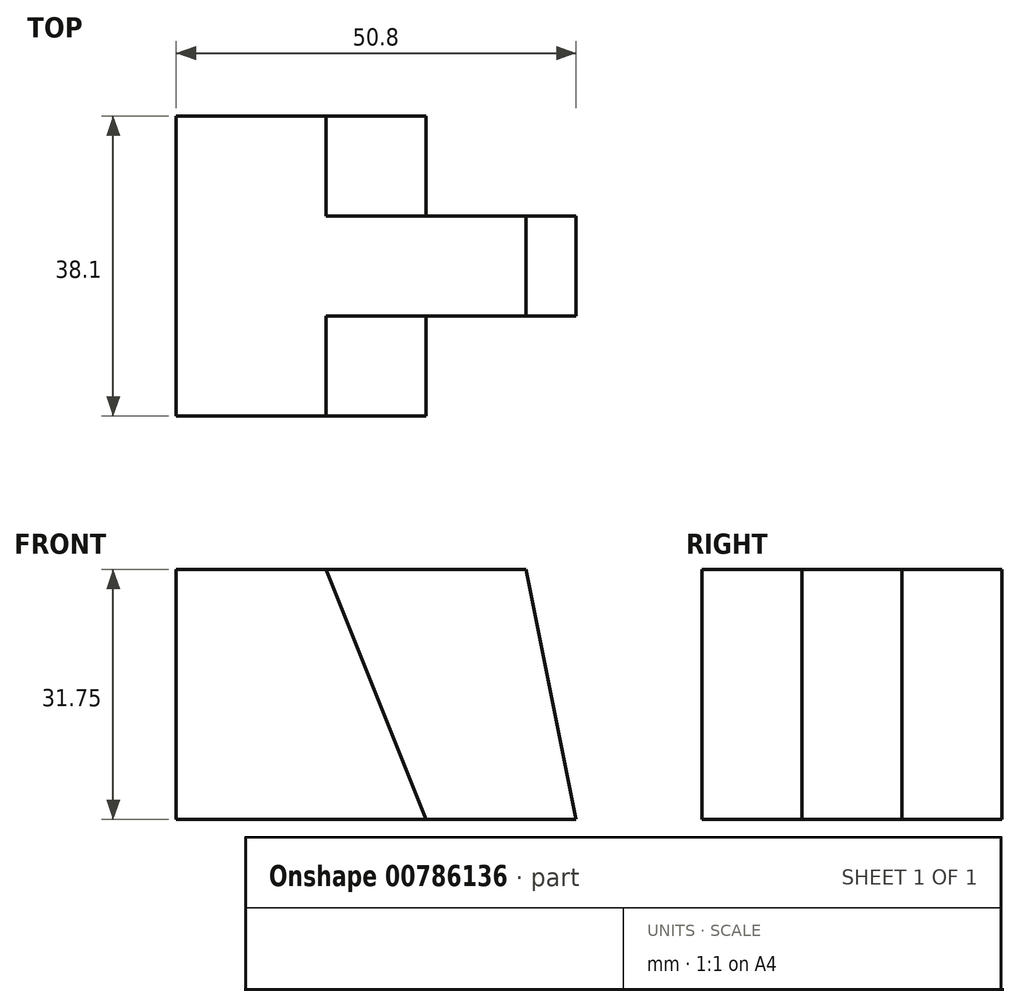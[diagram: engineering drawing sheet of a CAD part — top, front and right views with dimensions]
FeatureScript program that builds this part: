
annotation { "Feature Type Name" : "Feature", "Feature Type Description" : "" }
export const myFeature = defineFeature(function(context is Context, id is Id, definition is map)
    precondition{}
    {
        {
            var Q0;
            Q0=qCreatedBy(makeId("Top.planeOp"),FACE);
            var sketch = newSketch(context, id + "F0", { "sketchPlane" : qUnion([Q0])});
            skLineSegment(sketch, "E0", {"start": v(0, 0) * mm, "end": v(0, 38.1) * mm});
            skLineSegment(sketch, "E1", {"start": v(0, 38.1) * mm, "end": v(50.8, 38.1) * mm});
            skLineSegment(sketch, "E2", {"start": v(0, 0) * mm, "end": v(50.8, 0) * mm});
            skLineSegment(sketch, "E3", {"start": v(50.8, 0) * mm, "end": v(50.8, 38.1) * mm});
            skSolve(sketch);
        }
        {
            var Q0;
            Q0=makeQuery(id+"F0.imprint","IMPRINT",FACE,{"disambiguationData":[TD([[makeQuery(id+"F0.imprint","IMPRINT",EDGE,{"derivedFrom":sQuery(id+"F0.wireOp",EDGE,"E0")}),-1.0]])]});
            extrude(context, id + "F1", {"entities" : qUnion([Q0]), "depth" : 31.75 * mm, "offsetDistance" : 25.4 * mm});
        }
        {
            var Q0;
            Q0=makeQuery(id+"F1.opExtrude","SWEPT_FACE",FACE,{"disambiguationData":[OSD([sQuery(id+"F0.wireOp",EDGE,"E2")])]});
            var sketch = newSketch(context, id + "F2", { "sketchPlane" : qUnion([Q0])});
            skLineSegment(sketch, "E4", {"start": v(0, 0) * mm, "end": v(31.75, 0) * mm});
            skLineSegment(sketch, "E5", {"start": v(0, 31.75) * mm, "end": v(19.05, 31.75) * mm});
            skLineSegment(sketch, "E6", {"start": v(19.05, 31.75) * mm, "end": v(31.75, 0) * mm});
            skSolve(sketch);
        }
        {
            var Q0;
            {var subQ0=sQuery(id+"F2.wireOp",EDGE,"E6");Q0=makeQuery(id+"F2.imprint","IMPRINT",FACE,{"disambiguationData":[TD([[makeQuery(id+"F2.imprint","IMPRINT",EDGE,{"derivedFrom":subQ0}),1.0]])]});}
            extrude(context, id + "F3", {"entities" : qUnion([Q0]), "operationType" : NewBodyOperationType.REMOVE, "oppositeDirection" : true, "depth" : 12.7 * mm, "offsetDistance" : 25.4 * mm});
        }
        {
            var Q0;
            Q0=makeQuery(id+"F1.opExtrude","SWEPT_FACE",FACE,{"disambiguationData":[OSD([sQuery(id+"F0.wireOp",EDGE,"E1")])]});
            var sketch = newSketch(context, id + "F4", { "sketchPlane" : qUnion([Q0])});
            skLineSegment(sketch, "E7", {"start": v(0, 0) * mm, "end": v(-31.75, 0) * mm});
            skLineSegment(sketch, "E8", {"start": v(0, 31.75) * mm, "end": v(-19.05, 31.75) * mm});
            skLineSegment(sketch, "E9", {"start": v(-19.05, 31.75) * mm, "end": v(-31.75, 0) * mm});
            skSolve(sketch);
        }
        {
            var Q0;
            {var subQ0=sQuery(id+"F4.wireOp",EDGE,"E9");Q0=makeQuery(id+"F4.imprint","IMPRINT",FACE,{"disambiguationData":[TD([[makeQuery(id+"F4.imprint","IMPRINT",EDGE,{"derivedFrom":subQ0}),-1.0]])]});}
            extrude(context, id + "F5", {"entities" : qUnion([Q0]), "operationType" : NewBodyOperationType.REMOVE, "oppositeDirection" : true, "depth" : 12.7 * mm, "offsetDistance" : 25.4 * mm});
        }
        {
            var Q0;
            Q0=makeQuery(id+"F3.boolean.opBoolean","COPY",FACE,{"derivedFrom":makeQuery(id+"F3.opExtrude","CAP_FACE",FACE,{"disambiguationData":[OSD([sQuery(id+"F0.wireOp",EDGE,"E2"),sQuery(id+"F0.wireOp",EDGE,"E3"),sQuery(id+"F2.wireOp",EDGE,"E6")])],"isStart":false})});
            var sketch = newSketch(context, id + "F6", { "sketchPlane" : qUnion([Q0])});
            skLineSegment(sketch, "E10", {"start": v(50.8, 0) * mm, "end": v(44.45, 31.75) * mm});
            skLineSegment(sketch, "E11", {"start": v(50.8, 31.75) * mm, "end": v(44.45, 31.75) * mm});
            skSolve(sketch);
        }
        {
            var Q0;
            Q0=makeQuery(id+"F6.imprint","IMPRINT",FACE,{"disambiguationData":[TD([[makeQuery(id+"F6.imprint","IMPRINT",EDGE,{"derivedFrom":sQuery(id+"F6.wireOp",EDGE,"E10")}),-1.0]])]});
            extrude(context, id + "F7", {"entities" : qUnion([Q0]), "operationType" : NewBodyOperationType.REMOVE, "oppositeDirection" : true, "depth" : 25.4 * mm, "offsetDistance" : 25.4 * mm});
        }
    });
